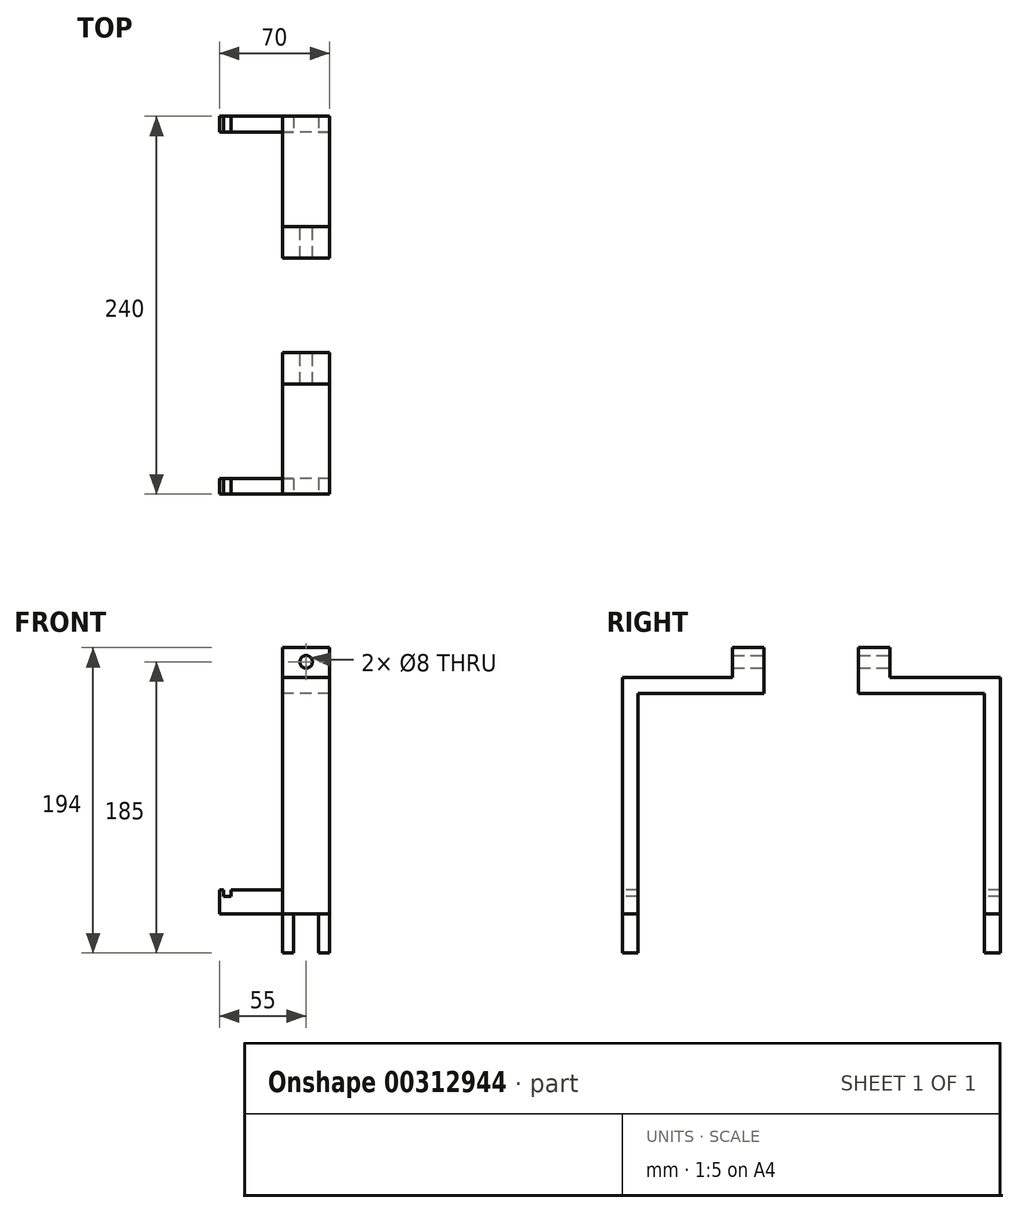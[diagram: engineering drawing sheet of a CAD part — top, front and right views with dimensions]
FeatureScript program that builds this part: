
annotation { "Feature Type Name" : "Feature", "Feature Type Description" : "" }
export const myFeature = defineFeature(function(context is Context, id is Id, definition is map)
    precondition{}
    {
        {
            var Q0;
            Q0=qCreatedBy(makeId("Right.planeOp"),FACE);
            var sketch = newSketch(context, id + "F0", { "sketchPlane" : qUnion([Q0])});
            skLineSegment(sketch, "E0", {"start": v(0, 0) * mm, "end": v(-110, 0) * mm, "construction": true});
            skLineSegment(sketch, "E1", {"start": v(0, 0) * mm, "end": v(110, 0) * mm, "construction": true});
            skLineSegment(sketch, "E2", {"start": v(-120, 0) * mm, "end": v(-110, 0) * mm});
            skLineSegment(sketch, "E3", {"start": v(110, 0) * mm, "end": v(110, 140) * mm});
            skLineSegment(sketch, "E4", {"start": v(110, 140) * mm, "end": v(30, 140) * mm});
            skLineSegment(sketch, "E5", {"start": v(30, 140) * mm, "end": v(30, 150) * mm});
            skLineSegment(sketch, "E6", {"start": v(30, 150) * mm, "end": v(120, 150) * mm});
            skLineSegment(sketch, "E7", {"start": v(120, 150) * mm, "end": v(120, 0) * mm});
            skLineSegment(sketch, "E8", {"start": v(120, 0) * mm, "end": v(110, 0) * mm});
            skLineSegment(sketch, "E9", {"start": v(-120, 0) * mm, "end": v(-120, 150) * mm});
            skLineSegment(sketch, "E10", {"start": v(-120, 150) * mm, "end": v(-30, 150) * mm});
            skLineSegment(sketch, "E11", {"start": v(-30, 150) * mm, "end": v(-30, 140) * mm});
            skLineSegment(sketch, "E12", {"start": v(-30, 140) * mm, "end": v(-110, 140) * mm});
            skLineSegment(sketch, "E13", {"start": v(-110, 140) * mm, "end": v(-110, 0) * mm});
            skLineSegment(sketch, "E14", {"start": v(-30, 150) * mm, "end": v(30, 150) * mm, "construction": true});
            skSolve(sketch);
        }
        {
            var Q0;
            Q0 = qSketchRegion(id + "F0", true);
            extrude(context, id + "F1", {"entities" : qUnion([Q0]), "depth" : 30 * mm});
        }
        {
            var Q0;
            Q0=makeQuery(id+"F1.opExtrude","SWEPT_FACE",FACE,{"disambiguationData":[OSD([sQuery(id+"F0.wireOp",EDGE,"E10")])]});
            var sketch = newSketch(context, id + "F2", { "sketchPlane" : qUnion([Q0])});
            skLineSegment(sketch, "E15", {"start": v(0, -30) * mm, "end": v(0, -50) * mm});
            skLineSegment(sketch, "E16", {"start": v(0, -50) * mm, "end": v(30, -50) * mm});
            skLineSegment(sketch, "E17", {"start": v(30, -50) * mm, "end": v(30, -30) * mm});
            skLineSegment(sketch, "E18", {"start": v(0, -30) * mm, "end": v(30, -30) * mm});
            skSolve(sketch);
        }
        {
            var Q0;
            Q0 = qSketchRegion(id + "F2", true);
            extrude(context, id + "F3", {"entities" : qUnion([Q0]), "operationType" : NewBodyOperationType.ADD, "depth" : 20 * mm});
        }
        {
            var Q0;
            Q0=makeQuery(id+"F1.opExtrude","SWEPT_FACE",FACE,{"disambiguationData":[OSD([sQuery(id+"F0.wireOp",EDGE,"E6")])]});
            var sketch = newSketch(context, id + "F4", { "sketchPlane" : qUnion([Q0])});
            skLineSegment(sketch, "E19", {"start": v(0, 30) * mm, "end": v(0, 50) * mm});
            skLineSegment(sketch, "E20", {"start": v(0, 50) * mm, "end": v(30, 50) * mm});
            skLineSegment(sketch, "E21", {"start": v(30, 50) * mm, "end": v(30, 30) * mm});
            skLineSegment(sketch, "E22", {"start": v(30, 30) * mm, "end": v(0, 30) * mm});
            skSolve(sketch);
        }
        {
            var Q0;
            Q0 = qSketchRegion(id + "F4", true);
            extrude(context, id + "F5", {"entities" : qUnion([Q0]), "operationType" : NewBodyOperationType.ADD, "depth" : 20 * mm});
        }
        {
            var Q0;
            Q0=makeQuery(id+"F5.opExtrude","SWEPT_FACE",FACE,{"disambiguationData":[OSD([sQuery(id+"F4.wireOp",EDGE,"E20")])]});
            var sketch = newSketch(context, id + "F6", { "sketchPlane" : qUnion([Q0])});
            skLineSegment(sketch, "E23", {"start": v(-15, 170) * mm, "end": v(-15, 160) * mm, "construction": true});
            skPoint(sketch, "E23.endSnap0", {"position": v(-30, 160) * mm});
            skSolve(sketch);
        }
        {
            var Q0;
            Q0=sQuery(id+"F6.wireOp",VERTEX,"E23.end");
            var Q1;
            Q1=makeQuery(id+"F1.opExtrude","SWEPT_BODY",BODY,{"disambiguationData":[OSD([sQuery(id+"F0.wireOp",EDGE,"E2"),sQuery(id+"F0.wireOp",EDGE,"E9"),sQuery(id+"F0.wireOp",EDGE,"E10"),sQuery(id+"F0.wireOp",EDGE,"E11"),sQuery(id+"F0.wireOp",EDGE,"E12"),sQuery(id+"F0.wireOp",EDGE,"E13")])]});
            var Q2;
            Q2=makeQuery(id+"F1.opExtrude","SWEPT_BODY",BODY,{"disambiguationData":[OSD([sQuery(id+"F0.wireOp",EDGE,"E3"),sQuery(id+"F0.wireOp",EDGE,"E4"),sQuery(id+"F0.wireOp",EDGE,"E5"),sQuery(id+"F0.wireOp",EDGE,"E6"),sQuery(id+"F0.wireOp",EDGE,"E7"),sQuery(id+"F0.wireOp",EDGE,"E8")])]});
            hole(context, id + "F7", {"style" : HoleStyle.SIMPLE, "endStyle" : HoleEndStyle.THROUGH, "holeDiameter" : 8 * mm, "tappedDepth" : 12 * mm, "tapClearance" : 3, "locations" : qUnion([Q0]), "scope" : qUnion([Q1, Q2])});
        }
        {
            var Q0;
            Q0=makeQuery(id+"F1.opExtrude","SWEPT_FACE",FACE,{"disambiguationData":[OSD([sQuery(id+"F0.wireOp",EDGE,"E8")])]});
            var sketch = newSketch(context, id + "F8", { "sketchPlane" : qUnion([Q0])});
            skLineSegment(sketch, "E24", {"start": v(30, -110) * mm, "end": v(23, -110) * mm});
            skLineSegment(sketch, "E25", {"start": v(23, -110) * mm, "end": v(23, -120) * mm});
            skLineSegment(sketch, "E26", {"start": v(23, -120) * mm, "end": v(30, -120) * mm});
            skLineSegment(sketch, "E27", {"start": v(30, -120) * mm, "end": v(30, -110) * mm});
            skLineSegment(sketch, "E28", {"start": v(0, -110) * mm, "end": v(7, -110) * mm});
            skLineSegment(sketch, "E29", {"start": v(7, -110) * mm, "end": v(7, -120) * mm});
            skLineSegment(sketch, "E30", {"start": v(7, -120) * mm, "end": v(0, -120) * mm});
            skLineSegment(sketch, "E31", {"start": v(0, -120) * mm, "end": v(0, -110) * mm});
            skLineSegment(sketch, "E32", {"start": v(30, -110) * mm, "end": v(30, 110) * mm, "construction": true});
            skLineSegment(sketch, "E33", {"start": v(30, 110) * mm, "end": v(30, 120) * mm});
            skLineSegment(sketch, "E34", {"start": v(0, 120) * mm, "end": v(0, 110) * mm});
            skLineSegment(sketch, "E35", {"start": v(30, 120) * mm, "end": v(23, 120) * mm});
            skLineSegment(sketch, "E36", {"start": v(23, 120) * mm, "end": v(23, 110) * mm});
            skLineSegment(sketch, "E37", {"start": v(23, 110) * mm, "end": v(30, 110) * mm});
            skLineSegment(sketch, "E38", {"start": v(0, 120) * mm, "end": v(7, 120) * mm});
            skLineSegment(sketch, "E39", {"start": v(7, 120) * mm, "end": v(7, 110) * mm});
            skLineSegment(sketch, "E40", {"start": v(7, 110) * mm, "end": v(0, 110) * mm});
            skSolve(sketch);
        }
        {
            var Q0;
            Q0 = qSketchRegion(id + "F8", true);
            extrude(context, id + "F9", {"entities" : qUnion([Q0]), "depth" : 30 * mm});
        }
        {
            var Q0;
            Q0=makeQuery(id+"F5.boolean.opBoolean","MERGE",FACE,{"derivedFrom":[makeQuery(id+"F1.opExtrude","CAP_FACE",FACE,{"disambiguationData":[OSD([sQuery(id+"F0.wireOp",EDGE,"E3"),sQuery(id+"F0.wireOp",EDGE,"E4"),sQuery(id+"F0.wireOp",EDGE,"E5"),sQuery(id+"F0.wireOp",EDGE,"E6"),sQuery(id+"F0.wireOp",EDGE,"E7"),sQuery(id+"F0.wireOp",EDGE,"E8")])],"isStart":true}),makeQuery(id+"F5.opExtrude","SWEPT_FACE",FACE,{"disambiguationData":[OSD([sQuery(id+"F4.wireOp",EDGE,"E19")])]})]});
            var sketch = newSketch(context, id + "F10", { "sketchPlane" : qUnion([Q0])});
            skLineSegment(sketch, "E41", {"start": v(-110, 0) * mm, "end": v(-120, 0) * mm});
            skLineSegment(sketch, "E42", {"start": v(-120, 0) * mm, "end": v(-120, 15) * mm});
            skLineSegment(sketch, "E43", {"start": v(-120, 15) * mm, "end": v(-110, 15) * mm});
            skLineSegment(sketch, "E44", {"start": v(-110, 15) * mm, "end": v(-110, 0) * mm});
            skLineSegment(sketch, "E45", {"start": v(0, 0) * mm, "end": v(-110, 0) * mm, "construction": true});
            skLineSegment(sketch, "E46", {"start": v(0, 0) * mm, "end": v(110, 0) * mm, "construction": true});
            skLineSegment(sketch, "E47", {"start": v(110, 0) * mm, "end": v(110, 15) * mm});
            skLineSegment(sketch, "E48", {"start": v(110, 15) * mm, "end": v(120, 15) * mm});
            skLineSegment(sketch, "E49", {"start": v(120, 15) * mm, "end": v(120, 0) * mm});
            skLineSegment(sketch, "E50", {"start": v(120, 0) * mm, "end": v(110, 0) * mm});
            skSolve(sketch);
        }
        {
            var Q0;
            Q0 = qSketchRegion(id + "F10", true);
            extrude(context, id + "F11", {"entities" : qUnion([Q0]), "depth" : 40 * mm});
        }
        {
            var Q0;
            Q0=makeQuery(id+"F11.opExtrude","SWEPT_FACE",FACE,{"disambiguationData":[OSD([sQuery(id+"F10.wireOp",EDGE,"E49")])]});
            var sketch = newSketch(context, id + "F12", { "sketchPlane" : qUnion([Q0])});
            skLineSegment(sketch, "E51", {"start": v(0, 15) * mm, "end": v(-32.5, 15) * mm, "construction": true});
            skLineSegment(sketch, "E52", {"start": v(-32.5, 15) * mm, "end": v(-37.5, 15) * mm});
            skLineSegment(sketch, "E53", {"start": v(-37.5, 15) * mm, "end": v(-37.5, 11) * mm});
            skLineSegment(sketch, "E54", {"start": v(-37.5, 11) * mm, "end": v(-32.5, 11) * mm});
            skLineSegment(sketch, "E55", {"start": v(-32.5, 11) * mm, "end": v(-32.5, 15) * mm});
            skSolve(sketch);
        }
        {
            var Q0;
            Q0 = qSketchRegion(id + "F12", true);
            extrude(context, id + "F13", {"entities" : qUnion([Q0]), "operationType" : NewBodyOperationType.REMOVE, "endBound" : BoundingType.THROUGH_ALL, "oppositeDirection" : true, "depth" : 231.8 * mm});
        }
        {
            var Q0;
            Q0=makeQuery(id+"F11.opExtrude","SWEPT_FACE",FACE,{"disambiguationData":[OSD([sQuery(id+"F10.wireOp",EDGE,"E42")])]});
            var sketch = newSketch(context, id + "F14", { "sketchPlane" : qUnion([Q0])});
            skLineSegment(sketch, "E56", {"start": v(40, 15) * mm, "end": v(37.5, 15) * mm, "construction": true});
            skLineSegment(sketch, "E57", {"start": v(37.5, 15) * mm, "end": v(32.5, 15) * mm});
            skLineSegment(sketch, "E58", {"start": v(32.5, 15) * mm, "end": v(32.5, 11) * mm});
            skLineSegment(sketch, "E59", {"start": v(32.5, 11) * mm, "end": v(37.5, 11) * mm});
            skLineSegment(sketch, "E60", {"start": v(37.5, 11) * mm, "end": v(37.5, 15) * mm});
            skSolve(sketch);
        }
        {
            var Q0;
            Q0 = qSketchRegion(id + "F14", true);
            extrude(context, id + "F15", {"entities" : qUnion([Q0]), "operationType" : NewBodyOperationType.REMOVE, "endBound" : BoundingType.THROUGH_ALL, "oppositeDirection" : true, "depth" : 25 * mm});
        }
        {
            var Q0;
            Q0=makeQuery(id+"F3.boolean.opBoolean","MERGE",FACE,{"derivedFrom":[makeQuery(id+"F1.opExtrude","CAP_FACE",FACE,{"disambiguationData":[OSD([sQuery(id+"F0.wireOp",EDGE,"E2"),sQuery(id+"F0.wireOp",EDGE,"E9"),sQuery(id+"F0.wireOp",EDGE,"E10"),sQuery(id+"F0.wireOp",EDGE,"E11"),sQuery(id+"F0.wireOp",EDGE,"E12"),sQuery(id+"F0.wireOp",EDGE,"E13")])],"isStart":false}),makeQuery(id+"F3.opExtrude","SWEPT_FACE",FACE,{"disambiguationData":[OSD([sQuery(id+"F2.wireOp",EDGE,"E17")])]})]});
            var sketch = newSketch(context, id + "F16", { "sketchPlane" : qUnion([Q0])});
            skLineSegment(sketch, "E61", {"start": v(-30, 170) * mm, "end": v(-30, -30) * mm, "construction": true});
            skLineSegment(sketch, "E62", {"start": v(-30, -30) * mm, "end": v(-110, -30) * mm, "construction": true});
            skLineSegment(sketch, "E63", {"start": v(-110, -30) * mm, "end": v(-110, -25) * mm, "construction": true});
            skLineSegment(sketch, "E64", {"start": v(-30, 170) * mm, "end": v(-30, 169) * mm, "construction": true});
            skLineSegment(sketch, "E65", {"start": v(-30, 169) * mm, "end": v(-57.16, 169) * mm});
            skLineSegment(sketch, "E66", {"start": v(-57.16, 169) * mm, "end": v(-57.16, 174.49) * mm});
            skLineSegment(sketch, "E67", {"start": v(-57.16, 174.49) * mm, "end": v(57.62, 174.49) * mm});
            skLineSegment(sketch, "E68", {"start": v(57.62, 174.49) * mm, "end": v(57.62, 169) * mm});
            skLineSegment(sketch, "E69", {"start": v(57.62, 169) * mm, "end": v(-30, 169) * mm});
            skLineSegment(sketch, "E70", {"start": v(-110, -25) * mm, "end": v(-131.81, -25) * mm});
            skLineSegment(sketch, "E71", {"start": v(-131.81, -25) * mm, "end": v(-131.81, -34.27) * mm});
            skLineSegment(sketch, "E72", {"start": v(-131.81, -34.27) * mm, "end": v(137.2, -34.27) * mm});
            skLineSegment(sketch, "E73", {"start": v(137.2, -34.27) * mm, "end": v(137.2, -25) * mm});
            skLineSegment(sketch, "E74", {"start": v(137.2, -25) * mm, "end": v(-110, -25) * mm});
            skSolve(sketch);
        }
        {
            var Q0;
            Q0 = qSketchRegion(id + "F16", true);
            extrude(context, id + "F17", {"entities" : qUnion([Q0]), "operationType" : NewBodyOperationType.REMOVE, "oppositeDirection" : true, "depth" : 69 * mm});
        }
    });
